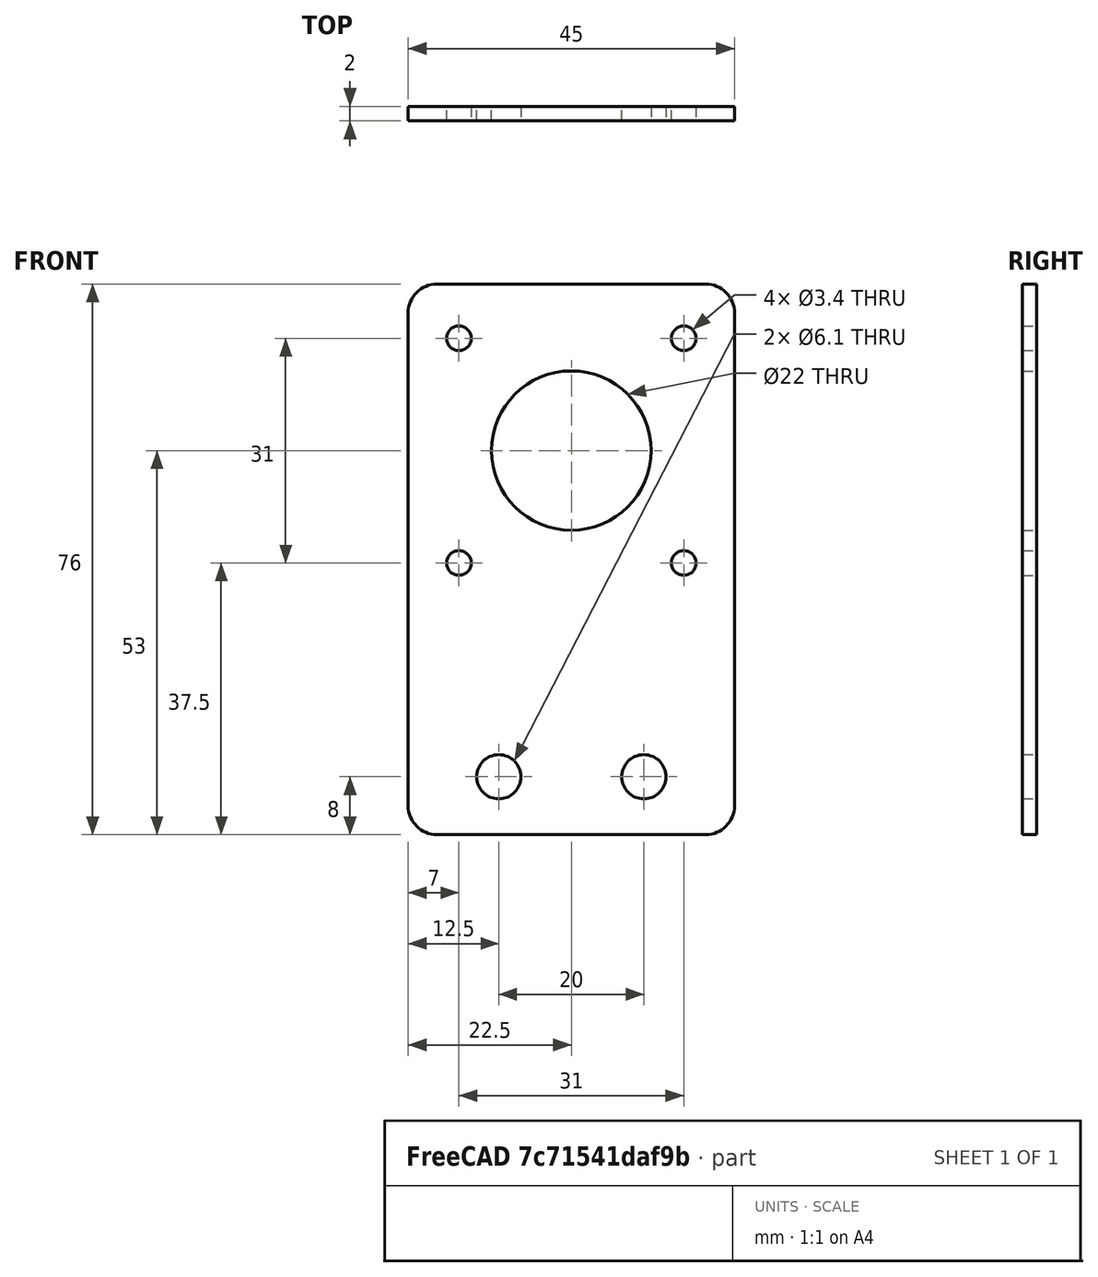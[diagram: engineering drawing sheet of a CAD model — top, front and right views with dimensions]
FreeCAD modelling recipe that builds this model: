
FCSTD DOCUMENT  (FreeCAD 0.15R4671 (Git))
Label: Plaque_moteur
License: All rights reserved
LicenseURL: http://en.wikipedia.org/wiki/All_rights_reserved
objects: Sketcher::SketchObject×1, PartDesign::Pad×1
note: 3 computed .brp shape members not serialized (recipe doc carries the construction recipe); baked Part::Feature solids carry a one-line shape summary decoded from their .brp

FEATURE [Sketcher::SketchObject] Sketch
  Placement = pos=(0,0,0) rot=(1,0,0;1.5708rad)
  sketch-geometry (15):
    g0: Circle CenterX=0 CenterY=0 CenterZ=0 NormalX=0 NormalY=0 NormalZ=1 Radius=11
    g1: Circle CenterX=-15.5 CenterY=15.5 CenterZ=0 NormalX=0 NormalY=0 NormalZ=1 Radius=1.7
    g2: Circle CenterX=15.5 CenterY=15.5 CenterZ=0 NormalX=0 NormalY=0 NormalZ=1 Radius=1.7
    g3: Circle CenterX=-15.5 CenterY=-15.5 CenterZ=0 NormalX=0 NormalY=0 NormalZ=1 Radius=1.7
    g4: Circle CenterX=15.5 CenterY=-15.5 CenterZ=0 NormalX=0 NormalY=0 NormalZ=1 Radius=1.7
    g5: Circle CenterX=-10 CenterY=-45 CenterZ=0 NormalX=0 NormalY=0 NormalZ=1 Radius=3.05
    g6: Circle CenterX=10 CenterY=-45 CenterZ=0 NormalX=0 NormalY=0 NormalZ=1 Radius=3.05
    g7: LineSegment StartX=-22.5 StartY=19 StartZ=0 EndX=-22.5 EndY=-49 EndZ=0
    g8: ArcOfCircle CenterX=-18.5 CenterY=-49 CenterZ=0 NormalX=0 NormalY=0 NormalZ=1 Radius=4 StartAngle=3.14159 EndAngle=4.71239
    g9: LineSegment StartX=-18.5 StartY=-53 StartZ=0 EndX=18.5 EndY=-53 EndZ=0
    g10: ArcOfCircle CenterX=18.5 CenterY=-49 CenterZ=0 NormalX=0 NormalY=0 NormalZ=1 Radius=4 StartAngle=4.71239 EndAngle=6.28319
    g11: LineSegment StartX=22.5 StartY=-49 StartZ=0 EndX=22.5 EndY=19 EndZ=0
    g12: ArcOfCircle CenterX=18.5 CenterY=19 CenterZ=0 NormalX=0 NormalY=0 NormalZ=1 Radius=4 StartAngle=0 EndAngle=1.5708
    g13: LineSegment StartX=18.5 StartY=23 StartZ=0 EndX=-18.5 EndY=23 EndZ=0
    g14: ArcOfCircle CenterX=-18.5 CenterY=19 CenterZ=0 NormalX=0 NormalY=0 NormalZ=1 Radius=4 StartAngle=1.5708 EndAngle=3.14159
  constraints (37):
    c: Coincident(g0,g-1)
    c: Radius(g0) = 11
    c: Radius(g1) = 1.7
    c: Equal(g1,g2)
    c: Equal(g1,g3)
    c: Equal(g1,g4)
    c: Symmetric(g1,g2,g-2)
    c: Symmetric(g3,g4,g-2)
    c: Symmetric(g1,g3,g-1)
    c: DistanceY(g1,g3) = -31
    c: DistanceX(g1,g2) = 31
    c: Radius(g5) = 3.05
    c: Equal(g5,g6)
    c: Symmetric(g5,g6,g-2)
    c: DistanceX(g5,g6) = 20
    c: DistanceY(g-1,g5) = -45
    c: Vertical(g7)
    c: Tangent(g7,g8) = -1.5708
    c: Tangent(g8,g9) = -1.5708
    c: Tangent(g9,g10) = -1.5708
    c: Tangent(g10,g11) = -1.5708
    c: Tangent(g11,g12) = -1.5708
    c: Tangent(g12,g13) = -1.5708
    c: Tangent(g13,g14) = -1.5708
    c: Coincident(g14,g7)
    c: Tangent(g14,g7)
    c: Horizontal(g13)
    c: Vertical(g11)
    c: Horizontal(g9)
    c: Radius(g14) = 4
    c: Equal(g14,g12)
    c: Equal(g14,g10)
    c: Equal(g14,g8)
    c: Symmetric(g7,g11,g-2)
    c: DistanceY(g-1,g13) = 23
    c: DistanceY(g5,g8) = -8
    c: DistanceX(g7,g11) = 45
FEATURE [PartDesign::Pad] Pad
  Length = 2
  Length2 = 100
  Placement = pos=(0,0,0) rot=(1,0,0;1.5708rad)
  Sketch = -> Sketch
  Type = 0
